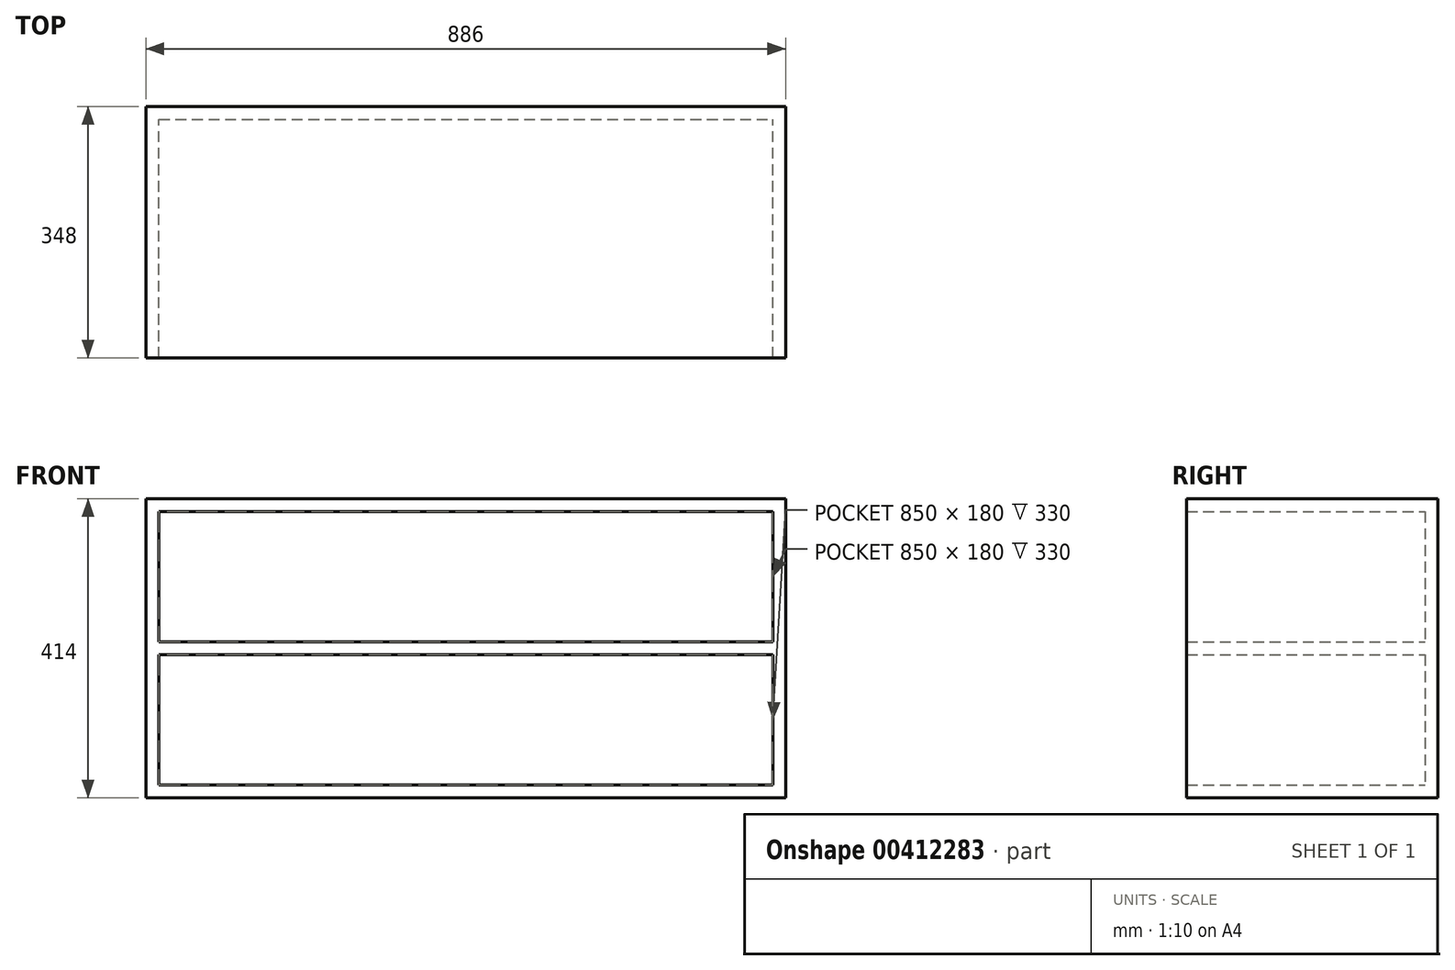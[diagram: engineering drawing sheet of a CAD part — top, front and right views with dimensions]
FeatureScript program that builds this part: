
annotation { "Feature Type Name" : "Feature", "Feature Type Description" : "" }
export const myFeature = defineFeature(function(context is Context, id is Id, definition is map)
    precondition{}
    {
        {
            var Q0;
            Q0=qCreatedBy(makeId("Front.planeOp"),FACE);
            var sketch = newSketch(context, id + "F0", { "sketchPlane" : qUnion([Q0])});
            skLineSegment(sketch, "E0.bottom", {"start": v(-443, 207) * mm, "end": v(443, 207) * mm});
            skLineSegment(sketch, "E0.top", {"start": v(-443, -207) * mm, "end": v(443, -207) * mm});
            skLineSegment(sketch, "E0.left", {"start": v(-443, 207) * mm, "end": v(-443, -207) * mm});
            skLineSegment(sketch, "E0.right", {"start": v(443, 207) * mm, "end": v(443, -207) * mm});
            skPoint(sketch, "E0.middle", {"position": v(0, 0) * mm});
            skLineSegment(sketch, "E1.0", {"start": v(-425, 189) * mm, "end": v(425, 189) * mm});
            skLineSegment(sketch, "E1.1", {"start": v(-425, 189) * mm, "end": v(-425, 9) * mm});
            skLineSegment(sketch, "E1.2", {"start": v(-425, -189) * mm, "end": v(425, -189) * mm});
            skLineSegment(sketch, "E1.3", {"start": v(425, 189) * mm, "end": v(425, 9) * mm});
            skLineSegment(sketch, "E2.bottom", {"start": v(-425, 9) * mm, "end": v(425, 9) * mm});
            skLineSegment(sketch, "E2.top", {"start": v(-425, -9) * mm, "end": v(425, -9) * mm});
            skLineSegment(sketch, "E3.trimOffspring", {"start": v(425, -9) * mm, "end": v(425, -189) * mm});
            skLineSegment(sketch, "E4.trimOffspring", {"start": v(-425, -9) * mm, "end": v(-425, -189) * mm});
            skSolve(sketch);
        }
        {
            var Q0;
            Q0 = qSketchRegion(id + "F0", true);
            extrude(context, id + "F1", {"entities" : qUnion([Q0]), "depth" : 330 * mm});
        }
        {
            var Q0;
            Q0=makeQuery(id+"F1.opExtrude","CAP_FACE",FACE,{"disambiguationData":[OSD([sQuery(id+"F0.wireOp",EDGE,"E0.bottom"),sQuery(id+"F0.wireOp",EDGE,"E0.top"),sQuery(id+"F0.wireOp",EDGE,"E0.left"),sQuery(id+"F0.wireOp",EDGE,"E0.right"),sQuery(id+"F0.wireOp",EDGE,"E1.0"),sQuery(id+"F0.wireOp",EDGE,"E1.1"),sQuery(id+"F0.wireOp",EDGE,"E1.2"),sQuery(id+"F0.wireOp",EDGE,"E1.3"),sQuery(id+"F0.wireOp",EDGE,"E2.bottom"),sQuery(id+"F0.wireOp",EDGE,"E2.top"),sQuery(id+"F0.wireOp",EDGE,"E3.trimOffspring"),sQuery(id+"F0.wireOp",EDGE,"E4.trimOffspring")])],"isStart":true});
            var sketch = newSketch(context, id + "F2", { "sketchPlane" : qUnion([Q0])});
            skLineSegment(sketch, "E5.bottom", {"start": v(-443, 207) * mm, "end": v(443, 207) * mm});
            skLineSegment(sketch, "E5.top", {"start": v(-443, -207) * mm, "end": v(443, -207) * mm});
            skLineSegment(sketch, "E5.left", {"start": v(-443, 207) * mm, "end": v(-443, -207) * mm});
            skLineSegment(sketch, "E5.right", {"start": v(443, 207) * mm, "end": v(443, -207) * mm});
            skSolve(sketch);
        }
        {
            var Q0;
            Q0 = qSketchRegion(id + "F2", true);
            extrude(context, id + "F3", {"entities" : qUnion([Q0]), "operationType" : NewBodyOperationType.ADD, "depth" : 18 * mm});
        }
    });
